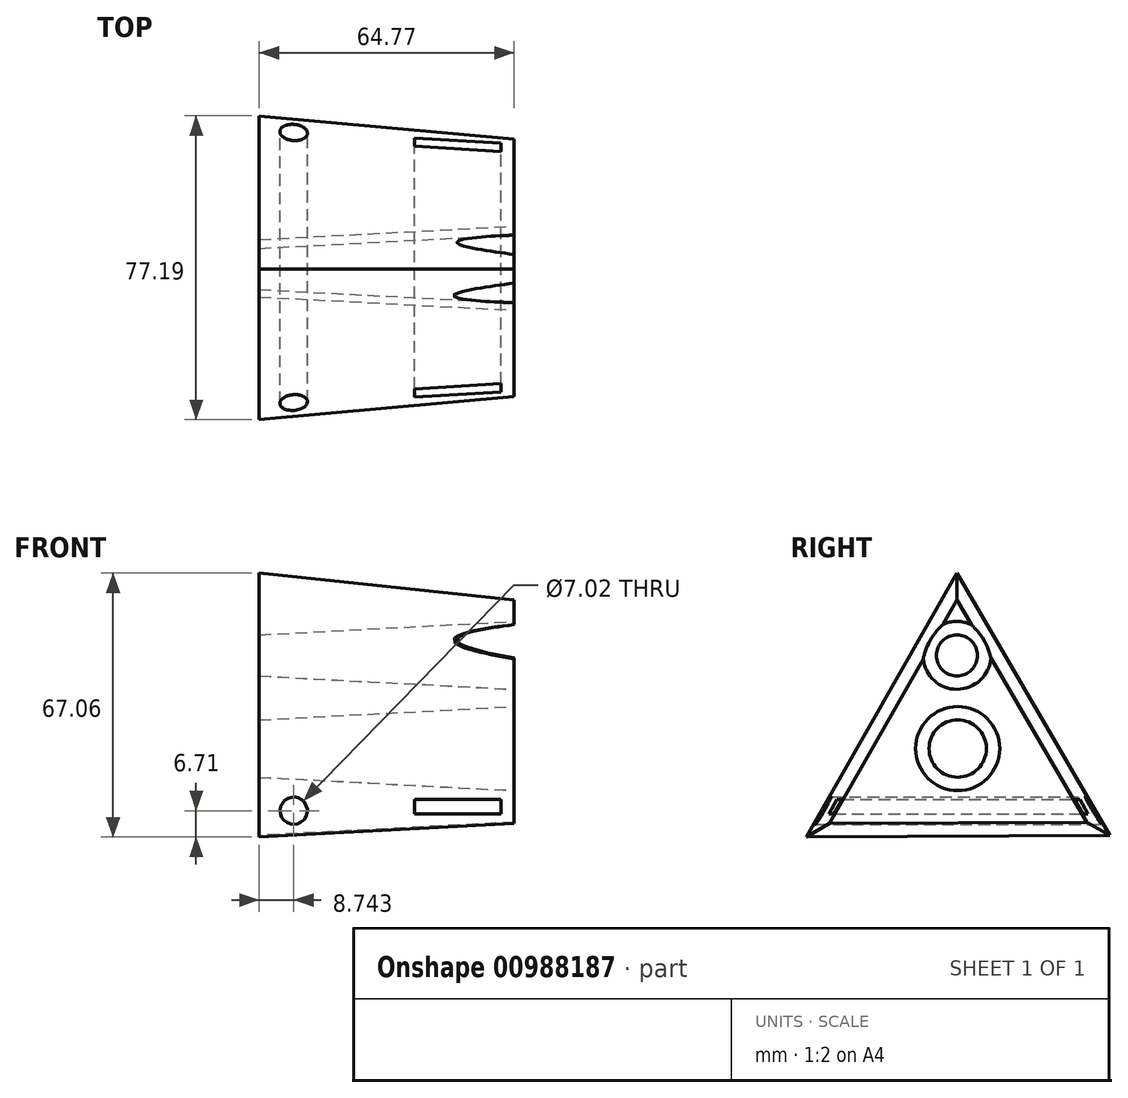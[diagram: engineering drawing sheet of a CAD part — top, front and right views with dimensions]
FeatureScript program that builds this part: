
annotation { "Feature Type Name" : "Feature", "Feature Type Description" : "" }
export const myFeature = defineFeature(function(context is Context, id is Id, definition is map)
    precondition{}
    {
        {
            var Q0;
            Q0=qCreatedBy(makeId("Right.planeOp"),FACE);
            var sketch = newSketch(context, id + "F0", { "sketchPlane" : qUnion([Q0])});
            skCircle(sketch, "E0.cCircle", {"center": v(0, 0) * mm, "radius": 44.57 * mm, "construction": true});
            skLineSegment(sketch, "E0.0", {"start": v(38.72, -22.07) * mm, "end": v(-38.47, -22.5) * mm});
            skLineSegment(sketch, "E0.1", {"start": v(-38.47, -22.5) * mm, "end": v(-0.24, 44.57) * mm});
            skLineSegment(sketch, "E0.2", {"start": v(-0.24, 44.57) * mm, "end": v(38.72, -22.07) * mm});
            skCircle(sketch, "E1", {"center": v(0, 0) * mm, "radius": 7.28 * mm});
            skLineSegment(sketch, "E2", {"start": v(-0.24, 44.57) * mm, "end": v(0, -38) * mm, "construction": true});
            skCircle(sketch, "E3", {"center": v(-0.18, 23.67) * mm, "radius": 5.23 * mm});
            skSolve(sketch);
        }
        {
            var Q0;
            Q0=makeQuery(id+"F0.imprint","IMPRINT",FACE,{"disambiguationData":[TD([[makeQuery(id+"F0.imprint","IMPRINT",EDGE,{"derivedFrom":sQuery(id+"F0.wireOp",EDGE,"E0.0")}),-1.0]])]});
            extrude(context, id + "F1", {"entities" : qUnion([Q0]), "depth" : 64.77 * mm, "offsetDistance" : 25.4 * mm, "hasDraft" : true, "draftAngle" : 3 * degree, "draftPullDirection" : true});
        }
        {
            var Q0;
            Q0=qCreatedBy(makeId("Front.planeOp"),FACE);
            var sketch = newSketch(context, id + "F2", { "sketchPlane" : qUnion([Q0])});
            skCircle(sketch, "E4", {"center": v(8.74, -15.78) * mm, "radius": 3.51 * mm});
            skLineSegment(sketch, "E5.bottom", {"start": v(61.48, -16.59) * mm, "end": v(39.5, -16.59) * mm});
            skLineSegment(sketch, "E5.top", {"start": v(61.48, -12.96) * mm, "end": v(39.5, -12.96) * mm});
            skLineSegment(sketch, "E5.left", {"start": v(61.48, -16.59) * mm, "end": v(61.48, -12.96) * mm});
            skLineSegment(sketch, "E5.right", {"start": v(39.5, -16.59) * mm, "end": v(39.5, -12.96) * mm});
            skPoint(sketch, "E5.middle", {"position": v(50.49, -14.77) * mm});
            skSolve(sketch);
        }
        {
            var Q0;
            Q0=qSketchRegion(id+"F2",true);
            extrude(context, id + "F3", {"entities" : qUnion([Q0]), "operationType" : NewBodyOperationType.REMOVE, "depth" : 120.9 * mm, "offsetDistance" : 25.4 * mm, "symmetric" : true});
        }
    });
